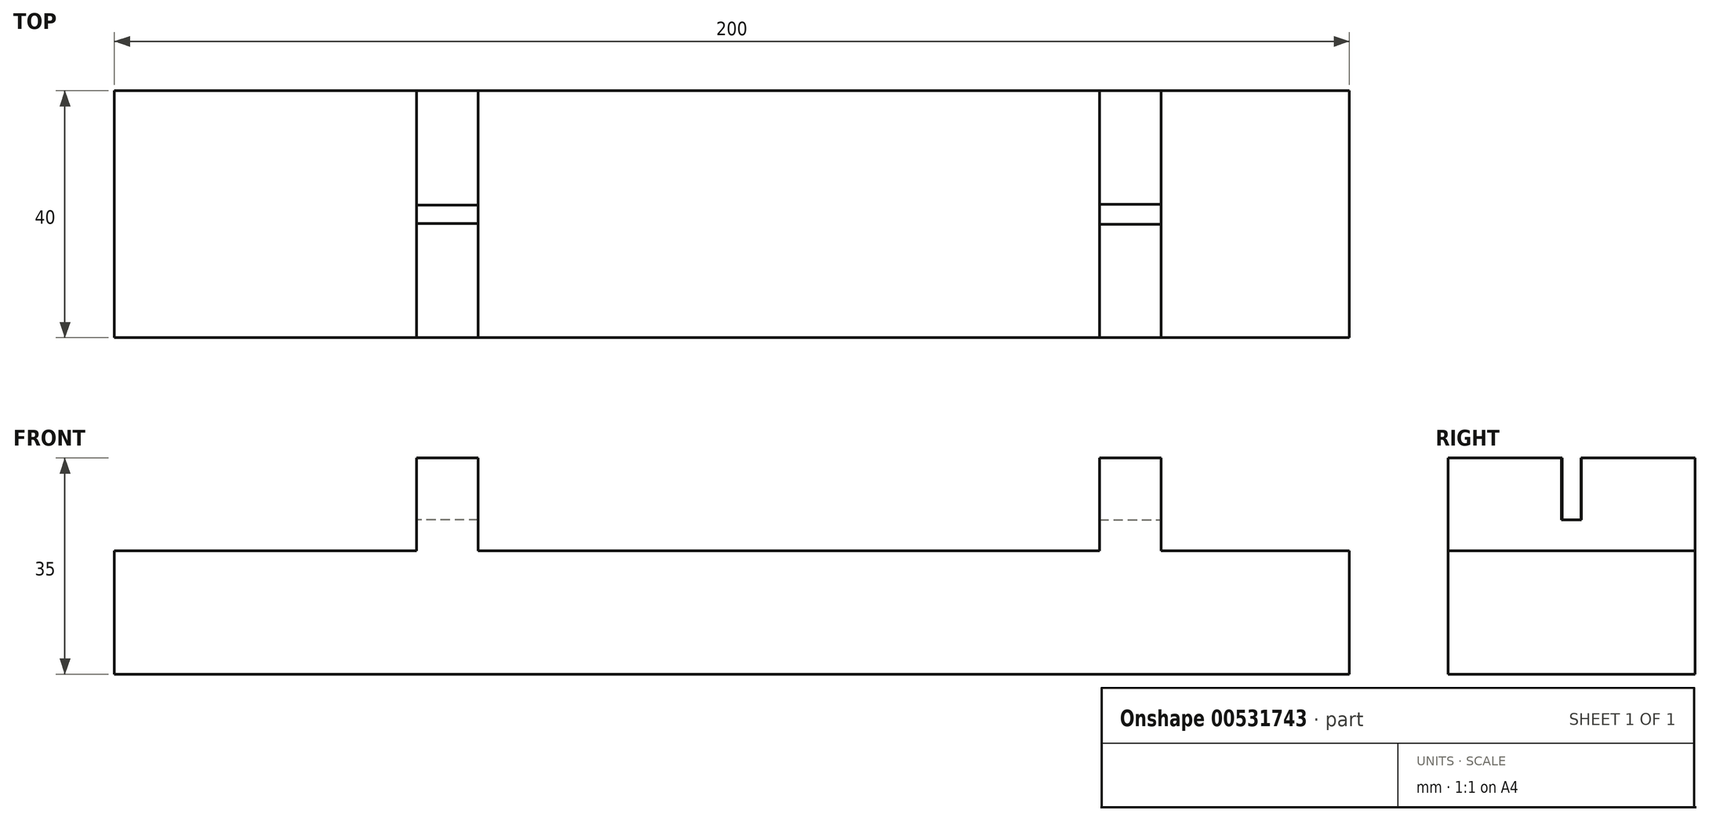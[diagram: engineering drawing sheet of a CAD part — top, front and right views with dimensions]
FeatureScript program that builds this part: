
annotation { "Feature Type Name" : "Feature", "Feature Type Description" : "" }
export const myFeature = defineFeature(function(context is Context, id is Id, definition is map)
    precondition{}
    {
        {
            var Q0;
            Q0=qCreatedBy(makeId("Front.planeOp"),FACE);
            var sketch = newSketch(context, id + "F0", { "sketchPlane" : qUnion([Q0])});
            skLineSegment(sketch, "E0.bottom", {"start": v(100, -10) * mm, "end": v(-100, -10) * mm});
            skLineSegment(sketch, "E0.top", {"start": v(100, 10) * mm, "end": v(-100, 10) * mm});
            skLineSegment(sketch, "E0.left", {"start": v(100, -10) * mm, "end": v(100, 10) * mm});
            skLineSegment(sketch, "E0.right", {"start": v(-100, -10) * mm, "end": v(-100, 10) * mm});
            skPoint(sketch, "E0.middle", {"position": v(0, 0) * mm});
            skSolve(sketch);
        }
        {
            var Q0;
            Q0=makeQuery(id+"F0.imprint","IMPRINT",FACE,{"disambiguationData":[TD([[makeQuery(id+"F0.imprint","IMPRINT",EDGE,{"derivedFrom":sQuery(id+"F0.wireOp",EDGE,"E0.bottom")}),-1.0]])]});
            extrude(context, id + "F1", {"entities" : qUnion([Q0]), "depth" : 40 * mm, "offsetDistance" : 25 * mm});
        }
        {
            var Q0;
            Q0=makeQuery(id+"F1.opExtrude","SWEPT_FACE",FACE,{"disambiguationData":[OSD([sQuery(id+"F0.wireOp",EDGE,"E0.top")])]});
            var sketch = newSketch(context, id + "F2", { "sketchPlane" : qUnion([Q0])});
            skLineSegment(sketch, "E1.bottom", {"start": v(59.53, -40) * mm, "end": v(69.53, -40) * mm});
            skLineSegment(sketch, "E1.top", {"start": v(59.53, 0) * mm, "end": v(69.53, 0) * mm});
            skLineSegment(sketch, "E1.left", {"start": v(59.53, -40) * mm, "end": v(59.53, 0) * mm});
            skLineSegment(sketch, "E1.right", {"start": v(69.53, -40) * mm, "end": v(69.53, 0) * mm});
            skLineSegment(sketch, "E2.bottom", {"start": v(-51.07, -40) * mm, "end": v(-41.07, -40) * mm});
            skLineSegment(sketch, "E2.top", {"start": v(-51.07, 0) * mm, "end": v(-41.07, 0) * mm});
            skLineSegment(sketch, "E2.left", {"start": v(-51.07, -40) * mm, "end": v(-51.07, 0) * mm});
            skLineSegment(sketch, "E2.right", {"start": v(-41.07, -40) * mm, "end": v(-41.07, 0) * mm});
            skSolve(sketch);
        }
        {
            var Q0;
            Q0=makeQuery(id+"F2.imprint","IMPRINT",FACE,{"disambiguationData":[TD([[makeQuery(id+"F2.imprint","IMPRINT",EDGE,{"derivedFrom":sQuery(id+"F2.wireOp",EDGE,"E1.bottom")}),-1.0]])]});
            extrude(context, id + "F3", {"entities" : qUnion([Q0]), "operationType" : NewBodyOperationType.ADD, "depth" : 10 * mm, "offsetDistance" : 25 * mm});
        }
        {
            var Q0;
            Q0 = qSketchRegion(id + "F2", true);
            extrude(context, id + "F4", {"entities" : qUnion([Q0]), "operationType" : NewBodyOperationType.ADD, "depth" : 15 * mm, "offsetDistance" : 25 * mm});
        }
        {
            var Q0;
            Q0=makeQuery(id+"F4.opExtrude","CAP_FACE",FACE,{"disambiguationData":[OSD([sQuery(id+"F2.wireOp",EDGE,"E2.bottom"),sQuery(id+"F2.wireOp",EDGE,"E2.top"),sQuery(id+"F2.wireOp",EDGE,"E2.left"),sQuery(id+"F2.wireOp",EDGE,"E2.right")])],"isStart":false});
            var sketch = newSketch(context, id + "F5", { "sketchPlane" : qUnion([Q0])});
            skLineSegment(sketch, "E3.bottom", {"start": v(-51.07, 0) * mm, "end": v(-41.07, 0) * mm});
            skLineSegment(sketch, "E4.bottom", {"start": v(-51.07, -40) * mm, "end": v(-41.07, -40) * mm});
            skLineSegment(sketch, "E5.bottom", {"start": v(-41.07, -40) * mm, "end": v(-51.07, -40) * mm});
            skLineSegment(sketch, "E5.top", {"start": v(-41.07, -21.5) * mm, "end": v(-51.07, -21.5) * mm});
            skLineSegment(sketch, "E5.left", {"start": v(-41.07, -40) * mm, "end": v(-41.07, -21.5) * mm});
            skLineSegment(sketch, "E5.right", {"start": v(-51.07, -40) * mm, "end": v(-51.07, -21.5) * mm});
            skLineSegment(sketch, "E6.top", {"start": v(-51.07, -18.5) * mm, "end": v(-41.07, -18.5) * mm});
            skLineSegment(sketch, "E6.left", {"start": v(-51.07, 0) * mm, "end": v(-51.07, -18.5) * mm});
            skLineSegment(sketch, "E6.right", {"start": v(-41.07, 0) * mm, "end": v(-41.07, -18.5) * mm});
            skLineSegment(sketch, "E7", {"start": v(-41.07, -18.5) * mm, "end": v(-41.07, -21.5) * mm});
            skLineSegment(sketch, "E8", {"start": v(-51.07, -18.5) * mm, "end": v(-51.07, -21.5) * mm});
            skSolve(sketch);
        }
        {
            var Q0;
            Q0=makeQuery(id+"F5.imprint","IMPRINT",FACE,{"disambiguationData":[TD([[makeQuery(id+"F5.imprint","IMPRINT",EDGE,{"derivedFrom":sQuery(id+"F5.wireOp",EDGE,"E5.top")}),-1.0]])]});
            extrude(context, id + "F6", {"entities" : qUnion([Q0]), "operationType" : NewBodyOperationType.REMOVE, "oppositeDirection" : true, "depth" : 10 * mm, "offsetDistance" : 25 * mm});
        }
        {
            var Q0;
            Q0=makeQuery(id+"F4.opExtrude","CAP_FACE",FACE,{"disambiguationData":[OSD([sQuery(id+"F2.wireOp",EDGE,"E1.bottom"),sQuery(id+"F2.wireOp",EDGE,"E1.top"),sQuery(id+"F2.wireOp",EDGE,"E1.left"),sQuery(id+"F2.wireOp",EDGE,"E1.right")])],"isStart":false});
            var sketch = newSketch(context, id + "F7", { "sketchPlane" : qUnion([Q0])});
            skLineSegment(sketch, "E9.bottom", {"start": v(59.53, 0) * mm, "end": v(69.53, 0) * mm});
            skLineSegment(sketch, "E9.top", {"start": v(59.53, -18.39) * mm, "end": v(69.53, -18.39) * mm});
            skLineSegment(sketch, "E9.left", {"start": v(59.53, 0) * mm, "end": v(59.53, -18.39) * mm});
            skLineSegment(sketch, "E9.right", {"start": v(69.53, 0) * mm, "end": v(69.53, -18.39) * mm});
            skLineSegment(sketch, "E10.bottom", {"start": v(59.53, -40) * mm, "end": v(69.53, -40) * mm});
            skLineSegment(sketch, "E10.top", {"start": v(59.53, -21.66) * mm, "end": v(69.53, -21.66) * mm});
            skLineSegment(sketch, "E10.left", {"start": v(59.53, -40) * mm, "end": v(59.53, -21.66) * mm});
            skLineSegment(sketch, "E10.right", {"start": v(69.53, -40) * mm, "end": v(69.53, -21.66) * mm});
            skLineSegment(sketch, "E11", {"start": v(59.53, -18.39) * mm, "end": v(59.53, 0) * mm});
            skLineSegment(sketch, "E12", {"start": v(69.53, -40) * mm, "end": v(59.53, -40) * mm});
            skLineSegment(sketch, "E13", {"start": v(59.53, -21.66) * mm, "end": v(59.53, -40) * mm});
            skSolve(sketch);
        }
        {
            var Q0;
            {var subQ0=sQuery(id+"F7.wireOp",EDGE,"E9.top");Q0=makeQuery(id+"F7.imprint","IMPRINT",FACE,{"disambiguationData":[TD([[makeQuery(id+"F7.imprint","IMPRINT",EDGE,{"derivedFrom":subQ0}),-1.0]])]});}
            extrude(context, id + "F8", {"entities" : qUnion([Q0]), "operationType" : NewBodyOperationType.REMOVE, "oppositeDirection" : true, "depth" : 10 * mm, "offsetDistance" : 25 * mm});
        }
    });
